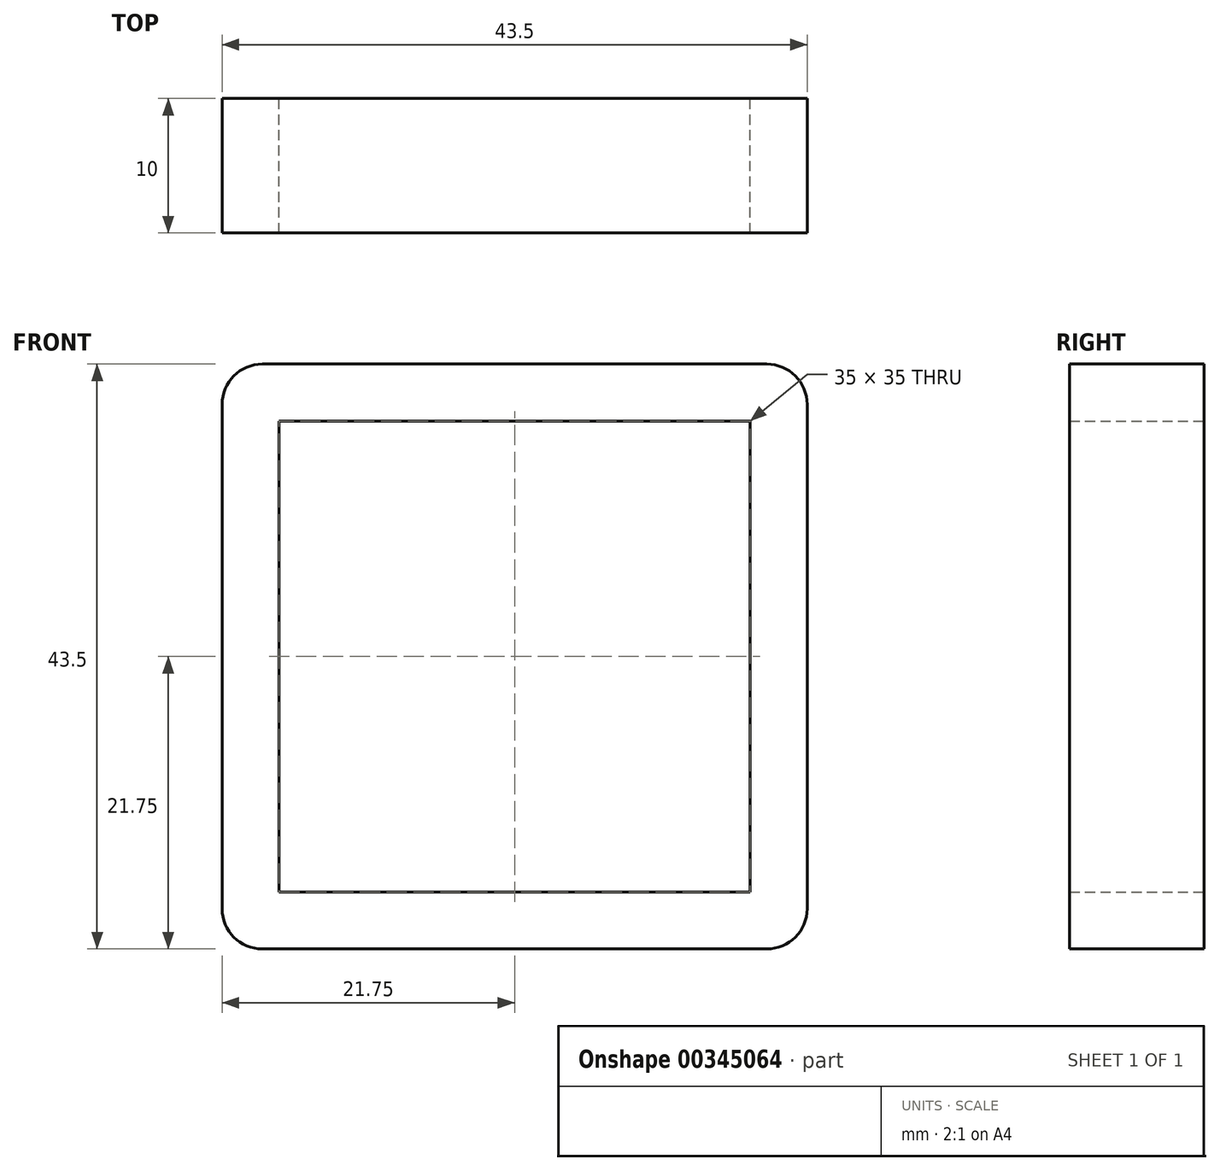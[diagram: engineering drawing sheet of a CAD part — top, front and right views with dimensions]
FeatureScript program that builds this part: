
annotation { "Feature Type Name" : "Feature", "Feature Type Description" : "" }
export const myFeature = defineFeature(function(context is Context, id is Id, definition is map)
    precondition{}
    {
        {
            var Q0;
            Q0=qCreatedBy(makeId("Front.planeOp"),FACE);
            var sketch = newSketch(context, id + "F0", { "sketchPlane" : qUnion([Q0])});
            skLineSegment(sketch, "E0.bottom", {"start": v(-21.75, 21.75) * mm, "end": v(21.75, 21.75) * mm});
            skLineSegment(sketch, "E0.top", {"start": v(-21.75, -21.75) * mm, "end": v(21.75, -21.75) * mm});
            skLineSegment(sketch, "E0.left", {"start": v(-21.75, 21.75) * mm, "end": v(-21.75, -21.75) * mm});
            skLineSegment(sketch, "E0.right", {"start": v(21.75, 21.75) * mm, "end": v(21.75, -21.75) * mm});
            skPoint(sketch, "E0.middle", {"position": v(0, 0) * mm});
            skLineSegment(sketch, "E1.bottom", {"start": v(-17.5, 17.5) * mm, "end": v(17.5, 17.5) * mm});
            skLineSegment(sketch, "E1.top", {"start": v(-17.5, -17.5) * mm, "end": v(17.5, -17.5) * mm});
            skLineSegment(sketch, "E1.left", {"start": v(-17.5, 17.5) * mm, "end": v(-17.5, -17.5) * mm});
            skLineSegment(sketch, "E1.right", {"start": v(17.5, 17.5) * mm, "end": v(17.5, -17.5) * mm});
            skSolve(sketch);
        }
        {
            var Q0;
            Q0=makeQuery(id+"F0.imprint","IMPRINT",FACE,{"disambiguationData":[TD([[makeQuery(id+"F0.imprint","IMPRINT",EDGE,{"derivedFrom":sQuery(id+"F0.wireOp",EDGE,"E0.bottom")}),-1.0]])]});
            extrude(context, id + "F1", {"entities" : qUnion([Q0]), "depth" : 10 * mm});
        }
        {
            var Q0;
            Q0=makeQuery(id+"F1.opExtrude","SWEPT_EDGE",EDGE,{"disambiguationData":[OSD([sQuery(id+"F0.wireOp",EDGE,"E0.bottom"),sQuery(id+"F0.wireOp",EDGE,"E0.left")])]});
            var Q1;
            Q1=makeQuery(id+"F1.opExtrude","SWEPT_EDGE",EDGE,{"disambiguationData":[OSD([sQuery(id+"F0.wireOp",EDGE,"E0.bottom"),sQuery(id+"F0.wireOp",EDGE,"E0.right")])]});
            var Q2;
            Q2=makeQuery(id+"F1.opExtrude","SWEPT_EDGE",EDGE,{"disambiguationData":[OSD([sQuery(id+"F0.wireOp",EDGE,"E0.top"),sQuery(id+"F0.wireOp",EDGE,"E0.right")])]});
            var Q3;
            Q3=makeQuery(id+"F1.opExtrude","SWEPT_EDGE",EDGE,{"disambiguationData":[OSD([sQuery(id+"F0.wireOp",EDGE,"E0.top"),sQuery(id+"F0.wireOp",EDGE,"E0.left")])]});
            fillet(context, id + "F2", {"entities" : qUnion([Q0, Q1, Q2, Q3]), "radius" : 3 * mm, "tangentPropagation" : true, "allowEdgeOverflow" : false});
        }
    });
